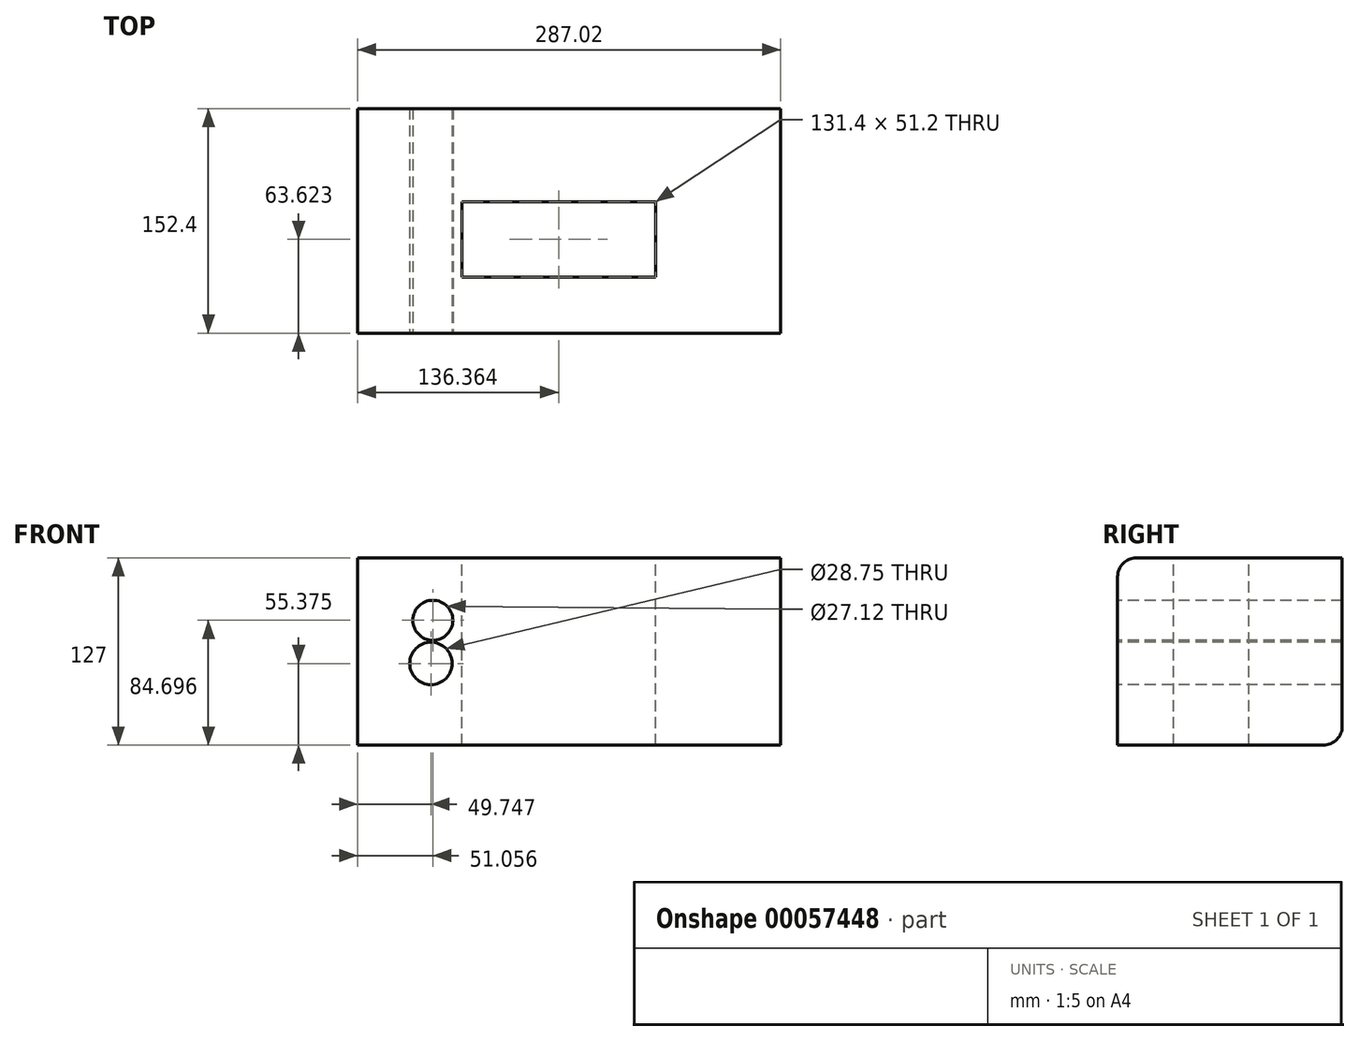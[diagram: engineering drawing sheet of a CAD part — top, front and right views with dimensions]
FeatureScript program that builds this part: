
annotation { "Feature Type Name" : "Feature", "Feature Type Description" : "" }
export const myFeature = defineFeature(function(context is Context, id is Id, definition is map)
    precondition{}
    {
        {
            var Q0;
            Q0=qCreatedBy(makeId("Front.planeOp"),FACE);
            var sketch = newSketch(context, id + "F0", { "sketchPlane" : qUnion([Q0])});
            skLineSegment(sketch, "E0.bottom", {"start": v(0, 0) * mm, "end": v(127, 0) * mm});
            skLineSegment(sketch, "E0.top", {"start": v(0, 127) * mm, "end": v(127, 127) * mm});
            skLineSegment(sketch, "E0.left", {"start": v(0, 0) * mm, "end": v(0, 127) * mm});
            skLineSegment(sketch, "E0.right", {"start": v(127, 0) * mm, "end": v(127, 127) * mm});
            skSolve(sketch);
        }
        {
            var Q0;
            Q0 = qSketchRegion(id + "F0", true);
            extrude(context, id + "F1", {"entities" : qUnion([Q0]), "endBound" : BoundingType.SYMMETRIC, "depth" : 152.4 * mm});
        }
        {
            var Q0;
            Q0=makeQuery(id+"F1.opExtrude","CAP_EDGE",EDGE,{"disambiguationData":[OSD([sQuery(id+"F0.wireOp",EDGE,"E0.top")])],"isStart":false});
            var Q1;
            Q1=makeQuery(id+"F1.opExtrude","CAP_EDGE",EDGE,{"disambiguationData":[OSD([sQuery(id+"F0.wireOp",EDGE,"E0.bottom")])],"isStart":true});
            fillet(context, id + "F2", {"entities" : qUnion([Q0, Q1]), "radius" : 12.7 * mm, "tangentPropagation" : true, "allowEdgeOverflow" : false});
        }
        {
            var Q0;
            Q0=makeQuery(id+"F1.opExtrude","CAP_FACE",FACE,{"disambiguationData":[OSD([sQuery(id+"F0.wireOp",EDGE,"E0.bottom"),sQuery(id+"F0.wireOp",EDGE,"E0.top"),sQuery(id+"F0.wireOp",EDGE,"E0.left"),sQuery(id+"F0.wireOp",EDGE,"E0.right")])],"isStart":false});
            var sketch = newSketch(context, id + "F3", { "sketchPlane" : qUnion([Q0])});
            skCircle(sketch, "E1", {"center": v(51.06, 84.7) * mm, "radius": 13.56 * mm});
            skCircle(sketch, "E2", {"center": v(49.75, 55.38) * mm, "radius": 14.38 * mm});
            skSolve(sketch);
        }
        {
            var Q0;
            Q0 = qSketchRegion(id + "F3", true);
            extrude(context, id + "F4", {"entities" : qUnion([Q0]), "operationType" : NewBodyOperationType.REMOVE, "flatOperationType" : FlatOperationType.REMOVE, "endBound" : BoundingType.UP_TO_NEXT, "oppositeDirection" : true, "offsetDistance" : 25.4 * mm, "depth" : 25.4 * mm, "domain" : OperationDomain.MODEL});
        }
        {
            var Q0;
            Q0=makeQuery(id+"F1.opExtrude","SWEPT_FACE",FACE,{"disambiguationData":[OSD([sQuery(id+"F0.wireOp",EDGE,"E0.right")])]});
            extrude(context, id + "F5", {"entities" : qUnion([Q0]), "operationType" : NewBodyOperationType.ADD, "depth" : 160.02 * mm});
        }
        {
            var Q0;
            {var subQ0=sQuery(id+"F0.wireOp",EDGE,"E0.right");var subQ1=sQuery(id+"F0.wireOp",EDGE,"E0.top");Q0=makeQuery(id+"F5.boolean.opBoolean","MERGE",FACE,{"derivedFrom":[makeQuery(id+"F1.opExtrude","SWEPT_FACE",FACE,{"disambiguationData":[OSD([subQ1])]}),makeQuery(id+"F5.opExtrude","SWEPT_FACE",FACE,{"disambiguationData":[OSD([subQ1,subQ0]),TDD([makeQuery(id+"F1.opExtrude","SWEPT_EDGE",EDGE,{"disambiguationData":[OSD([subQ1,subQ0])]})])]})]});}
            var sketch = newSketch(context, id + "F6", { "sketchPlane" : qUnion([Q0])});
            skLineSegment(sketch, "E3.bottom", {"start": v(70.66, 13.02) * mm, "end": v(202.07, 13.02) * mm});
            skLineSegment(sketch, "E3.top", {"start": v(70.66, -38.18) * mm, "end": v(202.07, -38.18) * mm});
            skLineSegment(sketch, "E3.left", {"start": v(70.66, 13.02) * mm, "end": v(70.66, -38.18) * mm});
            skLineSegment(sketch, "E3.right", {"start": v(202.07, 13.02) * mm, "end": v(202.07, -38.18) * mm});
            skSolve(sketch);
        }
        {
            var Q0;
            Q0 = qSketchRegion(id + "F6", true);
            extrude(context, id + "F7", {"entities" : qUnion([Q0]), "operationType" : NewBodyOperationType.REMOVE, "oppositeDirection" : true, "depth" : 211.84 * mm});
        }
    });
